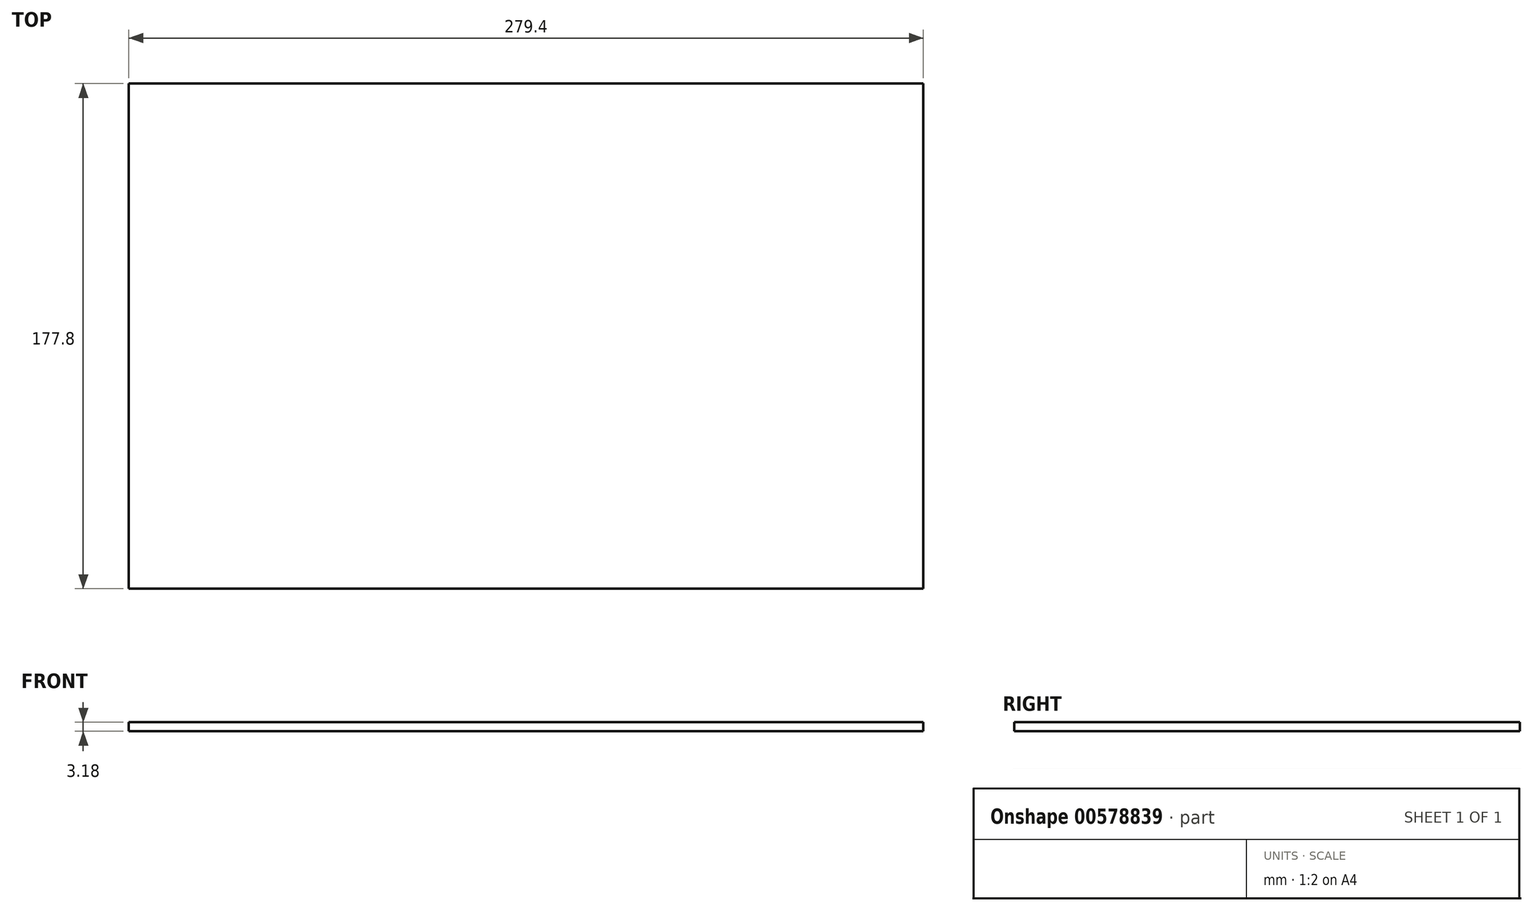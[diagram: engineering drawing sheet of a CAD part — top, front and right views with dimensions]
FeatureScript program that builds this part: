
annotation { "Feature Type Name" : "Feature", "Feature Type Description" : "" }
export const myFeature = defineFeature(function(context is Context, id is Id, definition is map)
    precondition{}
    {
        {
            var Q0;
            Q0=qCreatedBy(makeId("Front.planeOp"),FACE);
            var sketch = newSketch(context, id + "F0", { "sketchPlane" : qUnion([Q0])});
            skLineSegment(sketch, "E0.bottom", {"start": v(139.7, 1.59) * mm, "end": v(-139.7, 1.59) * mm});
            skLineSegment(sketch, "E0.top", {"start": v(139.7, -1.59) * mm, "end": v(-139.7, -1.59) * mm});
            skLineSegment(sketch, "E0.left", {"start": v(139.7, 1.59) * mm, "end": v(139.7, -1.59) * mm});
            skLineSegment(sketch, "E0.right", {"start": v(-139.7, 1.59) * mm, "end": v(-139.7, -1.59) * mm});
            skPoint(sketch, "E0.middle", {"position": v(0, 0) * mm});
            skSolve(sketch);
        }
        {
            var Q0;
            Q0=makeQuery(id+"F0.imprint","IMPRINT",FACE,{"disambiguationData":[TD([[makeQuery(id+"F0.imprint","IMPRINT",EDGE,{"derivedFrom":sQuery(id+"F0.wireOp",EDGE,"E0.bottom")}),1.0]])]});
            extrude(context, id + "F1", {"entities" : qUnion([Q0]), "depth" : 177.8 * mm, "offsetDistance" : 25.4 * mm});
        }
    });
